# Revit family: Слив СЛ-1,2
name_source: partatom
category: Обобщенные модели
revit_build: Autodesk Revit 2018 (Build: 20170630_0700(x64)
units: mm (PartAtom-declared; Revit-internal decimal feet)

## family parameters
Всегда вертикально = Нет
Может служить основой для арматурных стержней = Нет
На основе рабочей плоскости = Да
Общий = Да
При загрузке вырезать с полостями = Нет
Размер круглого соединителя = Использовать диаметр
Тип детали = Нормальный
Точка расчета площади = Нет

## types (2) — shared parameters
ADSK_Марка = Сл-2
ADSK_Масса = 1.25
ADSK_Наименование = Оцинкованный лист δ=0,8 мм, B=155 мм (или аналог)
ADSK_Обозначение = ГОСТ 598-90
ADSK_Примечание = СЛВ
Отметка по умолчанию = 1219 мм
Рзм.Ширина = 155 мм
Толщина листа = 1 мм
верхний загиб слива = 20 мм
диагональная длина = 110 мм
нижний загиб = 10 мм
последний угол = 113.00°
средний изгиб = 15 мм
угол второй = 75.00°
четверть = 50 мм
ширина слива = 55 мм

## per-type parameters (varying)
| type | угол |
| Сл-1 | 97.00° |
| Сл-2 | 95.00° |

## geometry (parser evidence)
native form markers: Blend x2
no freeform markers — native parametric forms only
